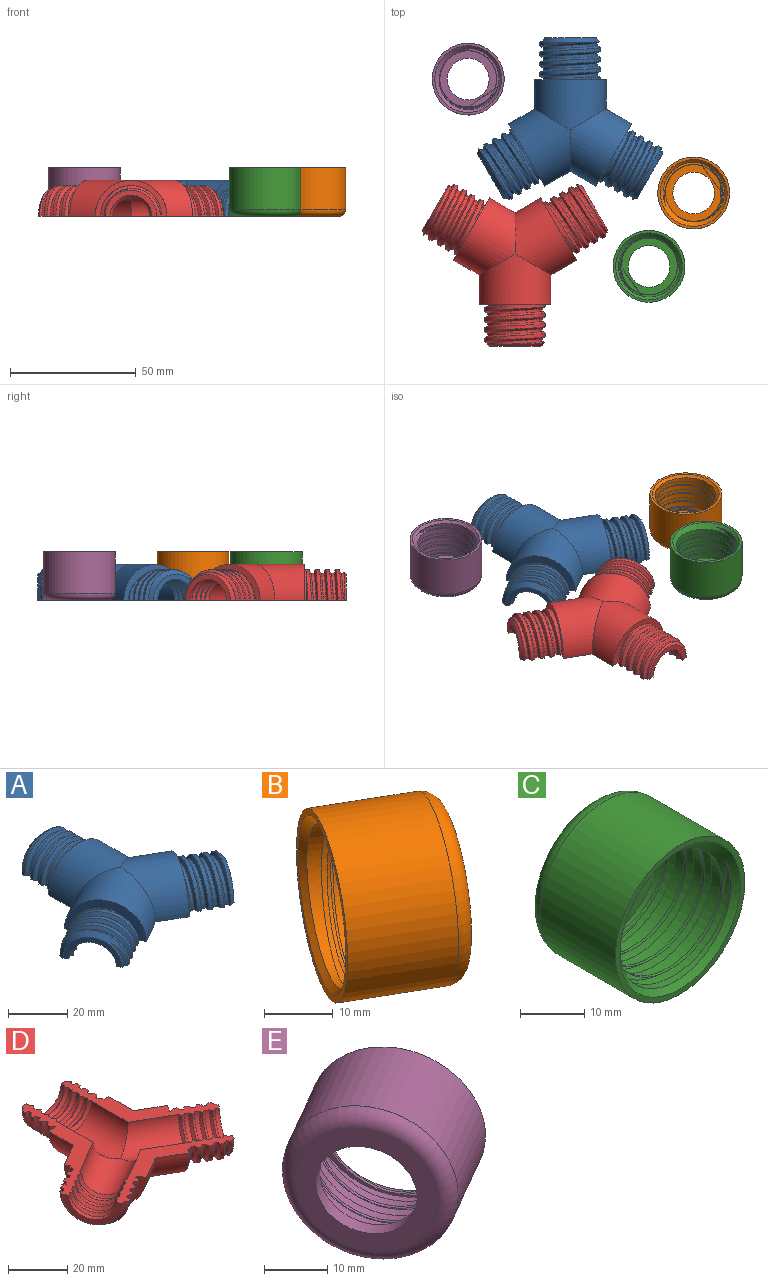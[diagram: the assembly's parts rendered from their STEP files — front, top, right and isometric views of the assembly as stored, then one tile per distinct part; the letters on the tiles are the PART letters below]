
ASSEMBLY  parts=5 mates=4
PART A: 114 faces, bbox 74.6x65.7x25.4 mm
  f0: extruded ~9.1x7.75mm, area 9.1mm2, adj f3,f4,f78,f107
  f1: extruded ~9.1x7.75mm, area 9.1mm2, adj f16,f17,f34,f75
  f2: extruded ~10.12x7.75mm, area 9.1mm2, adj f49,f50,f67,f74
  f3: bspline ~24.86x15.48mm, area 14.4mm2, adj f0,f78,f107,f111
  f4: plane 24.79x14.33mm, normal (-0.87,-0.5,0), area 125.8mm2, adj f0,f77,f78,f107,f111,f113
  f5: cone r=8.3mm half-angle=45deg, axis (0.87,-0.5,0), area 34.7mm2, adj f6,f37,f112,f113
  f6: cone r=7.3mm half-angle=45deg, axis (-0.87,0.5,0), area 34.7mm2, adj f5,f7,f112,f113
  f7: cylinder r=8.3mm len=15.18mm, axis (0.87,-0.5,0), area 41.7mm2, adj f6,f8,f112,f113
  f8: cone r=8.3mm half-angle=45deg, axis (0.87,-0.5,0), area 34.7mm2, adj f7,f9,f112,f113
  f9: cone r=7.3mm half-angle=45deg, axis (-0.87,0.5,0), area 34.7mm2, adj f8,f10,f112,f113
  f10: cylinder r=8.3mm len=15.18mm, axis (0.87,-0.5,0), area 41.7mm2, adj f9,f11,f112,f113
  f11: cone r=8.3mm half-angle=45deg, axis (0.87,-0.5,0), area 34.7mm2, adj f10,f12,f112,f113
  f12: cone r=7.3mm half-angle=45deg, axis (-0.87,0.5,0), area 34.7mm2, adj f11,f13,f112,f113
  f13: cylinder r=8.3mm len=15.18mm, axis (0.87,-0.5,0), area 41.7mm2, adj f12,f14,f112,f113
  f14: cone r=8.3mm half-angle=45deg, axis (0.87,-0.5,0), area 34.7mm2, adj f13,f15,f112,f113
  f15: cone r=7.3mm half-angle=45deg, axis (-0.87,0.5,0), area 34.7mm2, adj f14,f76,f112,f113
  f16: bspline ~24.86x16.81mm, area 14.4mm2, adj f1,f17,f34,f113
  f17: cylinder r=10.8mm len=20.06mm, axis (-0.87,0.5,0), area 40.6mm2, adj f1,f16,f18,f75,f112,f113
  f18: bspline ~24.86x22.64mm, area 58.5mm2, adj f17,f33,f112,f113
  f19: bspline ~24.86x22.47mm, area 60.7mm2, adj f20,f33,f112,f113
  f20: cylinder r=10.8mm len=20.27mm, axis (-0.87,0.5,0), area 38.5mm2, adj f19,f21,f112,f113
  f21: bspline ~24.86x22.64mm, area 58.5mm2, adj f20,f32,f112,f113
  f22: bspline ~24.86x22.47mm, area 60.7mm2, adj f23,f32,f112,f113
  f23: cylinder r=10.8mm len=20.27mm, axis (-0.87,0.5,0), area 38.5mm2, adj f22,f24,f112,f113
  f24: bspline ~24.86x22.64mm, area 58.5mm2, adj f23,f31,f112,f113
  f25: bspline ~21.3x6.91mm, area 8.7mm2, adj f26,f30,f35,f112
  f26: cylinder r=10.8mm len=8.69mm, axis (-0.87,0.5,0), area 3mm2, adj f25,f35,f112
  f27: bspline ~24.86x22.47mm, area 60.7mm2, adj f28,f31,f112,f113
  f28: cylinder r=10.8mm len=20.27mm, axis (-0.87,0.5,0), area 38.5mm2, adj f27,f29,f112,f113
  f29: bspline ~24.86x22.64mm, area 53.3mm2, adj f28,f30,f35,f112,f113
  f30: cylinder r=12.1mm len=17.62mm, axis (0.87,-0.5,0), area 19.1mm2, adj f25,f29,f35,f112
  f31: cylinder r=12.1mm len=22.64mm, axis (0.87,-0.5,0), area 51.9mm2, adj f24,f27,f112,f113
  f32: cylinder r=12.1mm len=22.64mm, axis (0.87,-0.5,0), area 51.9mm2, adj f21,f22,f112,f113
  f33: cylinder r=12.1mm len=22.64mm, axis (0.87,-0.5,0), area 51.9mm2, adj f18,f19,f112,f113
  f34: cylinder r=12.1mm len=2.93mm, axis (0.87,-0.5,0), area 2.2mm2, adj f1,f16,f75,f113
  f35: cone r=10.3mm half-angle=45deg, axis (-0.87,0.5,0), area 76.1mm2, adj f25,f26,f29,f30,f36,f112,f113
  f36: plane 17.84x10.3mm, normal (0.87,-0.5,0), area 58.4mm2, adj f35,f37,f112,f113
  f37: cylinder r=8.3mm len=15.18mm, axis (0.87,-0.5,0), area 41.7mm2, adj f5,f36,f112,f113
  f38: cone r=8.3mm half-angle=45deg, axis (0,1,0), area 34.7mm2, adj f39,f70,f111,f112
  f39: cone r=7.3mm half-angle=45deg, axis (0,-1,0), area 34.7mm2, adj f38,f40,f111,f112
  f40: cylinder r=8.3mm len=16.6mm, axis (0,1,0), area 41.7mm2, adj f39,f41,f111,f112
  f41: cone r=8.3mm half-angle=45deg, axis (0,1,0), area 34.7mm2, adj f40,f42,f111,f112
  f42: cone r=7.3mm half-angle=45deg, axis (0,-1,0), area 34.7mm2, adj f41,f43,f111,f112
  f43: cylinder r=8.3mm len=16.6mm, axis (0,1,0), area 41.7mm2, adj f42,f44,f111,f112
  f44: cone r=8.3mm half-angle=45deg, axis (0,1,0), area 34.7mm2, adj f43,f45,f111,f112
  f45: cone r=7.3mm half-angle=45deg, axis (0,-1,0), area 34.7mm2, adj f44,f46,f111,f112
  f46: cylinder r=8.3mm len=16.6mm, axis (0,1,0), area 41.7mm2, adj f45,f47,f111,f112
  f47: cone r=8.3mm half-angle=45deg, axis (0,1,0), area 34.7mm2, adj f46,f48,f111,f112
  f48: cone r=7.3mm half-angle=45deg, axis (0,-1,0), area 34.7mm2, adj f47,f71,f111,f112
  f49: bspline ~24.86x18.45mm, area 14.4mm2, adj f2,f50,f67,f112
  f50: cylinder r=10.8mm len=21.6mm, axis (0,-1,0), area 40.6mm2, adj f2,f49,f51,f74,f111,f112
  f51: bspline ~24.86x24.6mm, area 58.5mm2, adj f50,f66,f111,f112
  f52: bspline ~24.86x24.6mm, area 60.7mm2, adj f53,f66,f111,f112
  f53: cylinder r=10.8mm len=21.6mm, axis (0,-1,0), area 38.5mm2, adj f52,f54,f111,f112
  f54: bspline ~24.86x24.6mm, area 58.5mm2, adj f53,f65,f111,f112
  f55: bspline ~24.86x24.6mm, area 60.7mm2, adj f56,f65,f111,f112
  f56: cylinder r=10.8mm len=21.6mm, axis (0,-1,0), area 38.5mm2, adj f55,f57,f111,f112
  f57: bspline ~24.86x24.6mm, area 58.5mm2, adj f56,f64,f111,f112
  f58: bspline ~10.65x6.9mm, area 8.7mm2, adj f59,f63,f68,f111
  f59: cylinder r=10.8mm len=8.69mm, axis (0,-1,0), area 3mm2, adj f58,f68,f111
  f60: bspline ~24.86x24.6mm, area 60.7mm2, adj f61,f64,f111,f112
  f61: cylinder r=10.8mm len=21.6mm, axis (0,-1,0), area 38.5mm2, adj f60,f62,f111,f112
  f62: bspline ~24.86x24.6mm, area 53.3mm2, adj f61,f63,f68,f111,f112
  f63: cylinder r=12.1mm len=19.53mm, axis (0,1,0), area 19.1mm2, adj f58,f62,f68,f111
  f64: cylinder r=12.1mm len=24.2mm, axis (0,1,0), area 51.9mm2, adj f57,f60,f111,f112
  f65: cylinder r=12.1mm len=24.2mm, axis (0,1,0), area 51.9mm2, adj f54,f55,f111,f112
  f66: cylinder r=12.1mm len=24.2mm, axis (0,1,0), area 51.9mm2, adj f51,f52,f111,f112
  f67: cylinder r=12.1mm len=2.93mm, axis (0,1,0), area 2.2mm2, adj f2,f49,f74,f112
  f68: cone r=10.3mm half-angle=45deg, axis (0,-1,0), area 76.1mm2, adj f58,f59,f62,f63,f69,f111,f112
  f69: plane 20.6x10.3mm, normal (0,1,0), area 58.4mm2, adj f68,f70,f111,f112
  f70: cylinder r=8.3mm len=16.6mm, axis (0,1,0), area 41.7mm2, adj f38,f69,f111,f112
  f71: cylinder r=8.3mm len=22.27mm, axis (0,1,0), area 518.2mm2, adj f48,f76,f91,f111,f112
  f72: cylinder r=14.3mm len=28.6mm, axis (0,1,0), area 713mm2, adj f73,f74,f77,f111,f112
  f73: cylinder r=14.3mm len=34.77mm, axis (0.87,-0.5,0), area 713mm2, adj f72,f75,f77,f112,f113
  f74: plane 28.63x14.33mm, normal (0,1,0), area 125.8mm2, adj f2,f50,f67,f72,f111,f112
  f75: plane 24.79x14.33mm, normal (0.87,-0.5,0), area 125.8mm2, adj f1,f17,f34,f73,f112,f113
  f76: cylinder r=8.3mm len=27.59mm, axis (0.87,-0.5,0), area 518.2mm2, adj f15,f71,f91,f112,f113
  f77: cylinder r=14.3mm len=34.77mm, axis (-0.87,-0.5,0), area 713mm2, adj f4,f72,f73,f111,f113
  f78: cylinder r=10.8mm len=20.06mm, axis (0.87,0.5,0), area 40.6mm2, adj f0,f3,f4,f79,f111,f113
  f79: bspline ~24.86x20.64mm, area 58.5mm2, adj f78,f106,f111,f113
  f80: cone r=8.3mm half-angle=45deg, axis (-0.87,-0.5,0), area 34.7mm2, adj f81,f110,f111,f113
  f81: cone r=7.3mm half-angle=45deg, axis (0.87,0.5,0), area 34.7mm2, adj f80,f82,f111,f113
  f82: cylinder r=8.3mm len=15.18mm, axis (-0.87,-0.5,0), area 41.7mm2, adj f81,f83,f111,f113
  f83: cone r=8.3mm half-angle=45deg, axis (-0.87,-0.5,0), area 34.7mm2, adj f82,f84,f111,f113
  f84: cone r=7.3mm half-angle=45deg, axis (0.87,0.5,0), area 34.7mm2, adj f83,f85,f111,f113
  f85: cylinder r=8.3mm len=15.18mm, axis (-0.87,-0.5,0), area 41.7mm2, adj f84,f86,f111,f113
  f86: cone r=8.3mm half-angle=45deg, axis (-0.87,-0.5,0), area 34.7mm2, adj f85,f87,f111,f113
  f87: cone r=7.3mm half-angle=45deg, axis (0.87,0.5,0), area 34.7mm2, adj f86,f88,f111,f113
  f88: cylinder r=8.3mm len=15.18mm, axis (-0.87,-0.5,0), area 41.7mm2, adj f87,f89,f111,f113
  f89: cone r=8.3mm half-angle=45deg, axis (-0.87,-0.5,0), area 34.7mm2, adj f88,f90,f111,f113
  f90: cone r=7.3mm half-angle=45deg, axis (0.87,0.5,0), area 34.7mm2, adj f89,f91,f111,f113
  f91: cylinder r=8.3mm len=27.59mm, axis (-0.87,-0.5,0), area 518.2mm2, adj f71,f76,f90,f111,f113
  f92: bspline ~24.86x20.64mm, area 60.7mm2, adj f93,f106,f111,f113
  f93: cylinder r=10.8mm len=20.27mm, axis (0.87,0.5,0), area 38.5mm2, adj f92,f94,f111,f113
  f94: bspline ~24.86x20.64mm, area 58.5mm2, adj f93,f105,f111,f113
  f95: bspline ~24.86x20.64mm, area 60.7mm2, adj f96,f105,f111,f113
  f96: cylinder r=10.8mm len=20.27mm, axis (0.87,0.5,0), area 38.5mm2, adj f95,f97,f111,f113
  f97: bspline ~24.86x20.64mm, area 58.5mm2, adj f96,f104,f111,f113
  f98: bspline ~10.65x5.38mm, area 8.7mm2, adj f99,f103,f108,f113
  f99: cylinder r=10.8mm len=8.69mm, axis (0.87,0.5,0), area 3mm2, adj f98,f108,f113
  f100: bspline ~24.86x20.64mm, area 60.7mm2, adj f101,f104,f111,f113
  f101: cylinder r=10.8mm len=20.27mm, axis (0.87,0.5,0), area 38.5mm2, adj f100,f102,f111,f113
  f102: bspline ~24.86x20.64mm, area 53.3mm2, adj f101,f103,f108,f111,f113
  f103: cylinder r=12.1mm len=17.62mm, axis (-0.87,-0.5,0), area 19.1mm2, adj f98,f102,f108,f113
  f104: cylinder r=12.1mm len=22.64mm, axis (-0.87,-0.5,0), area 51.9mm2, adj f97,f100,f111,f113
  f105: cylinder r=12.1mm len=22.64mm, axis (-0.87,-0.5,0), area 51.9mm2, adj f94,f95,f111,f113
  f106: cylinder r=12.1mm len=22.64mm, axis (-0.87,-0.5,0), area 51.9mm2, adj f79,f92,f111,f113
  f107: cylinder r=12.1mm len=2.93mm, axis (-0.87,-0.5,0), area 2.2mm2, adj f0,f3,f4,f111
  f108: cone r=10.3mm half-angle=45deg, axis (0.87,0.5,0), area 76.1mm2, adj f98,f99,f102,f103,f109,f111,f113
  f109: plane 17.84x10.3mm, normal (-0.87,-0.5,0), area 58.4mm2, adj f108,f110,f111,f113
  f110: cylinder r=8.3mm len=15.18mm, axis (-0.87,-0.5,0), area 41.7mm2, adj f80,f109,f111,f113
  f111: plane 48.28x30.07mm, normal (0,0,-1), area 274.3mm2, adj f3,f4,f38,f39,f40,f41,f42,f43
  f112: plane 48.28x30.07mm, normal (0,0,-1), area 274.3mm2, adj f5,f6,f7,f8,f9,f10,f11,f12
  f113: plane 55.68x18.77mm, normal (0,0,-1), area 274.3mm2, adj f4,f5,f6,f7,f8,f9,f10,f11
PART B: 11 faces, bbox 30.5x34.4x31 mm
  f0: cylinder r=12.3mm len=29.14mm, axis (0.87,-0.5,0), area 682.7mm2, adj f4,f7,f10
  f1: torus R=11.74mm, axis (0.87,-0.5,0), area 338mm2, adj f2,f6
  f2: cylinder r=14.3mm len=33.1mm, axis (0.87,-0.5,0), area 1497.7mm2, adj f1,f3
  f3: plane 28.6x24.77mm, normal (-0.87,0.5,0), area 86.7mm2, adj f2,f10
  f4: plane 24x20.08mm, normal (-0.87,0.5,0), area 224mm2, adj f0,f5,f7,f8,f9
  f5: cylinder r=8.3mm len=16.6mm, axis (0.87,-0.5,0), area 133.6mm2, adj f4,f6
  f6: plane 23.48x20.33mm, normal (0.87,-0.5,0), area 216.4mm2, adj f1,f5
  f7: bspline ~11.79x8.2mm, area 6.6mm2, adj f0,f4,f8
  f8: extruded ~8.97x1.47mm, area 3.1mm2, adj f4,f7,f9
  f9: cylinder r=11.3mm len=26.91mm, axis (-0.87,0.5,0), area 151.3mm2, adj f4,f8,f10
  f10: cone r=15.3mm half-angle=45deg, axis (-0.87,0.5,0), area 143.6mm2, adj f0,f3,f9
PART C: 11 faces, bbox 31x19.2x31 mm
  f0: cylinder r=12.3mm len=24.6mm, axis (0,1,0), area 682.7mm2, adj f4,f7,f10
  f1: torus R=11.74mm, axis (0,1,0), area 338mm2, adj f2,f6
  f2: cylinder r=14.3mm len=28.6mm, axis (0,1,0), area 1497.7mm2, adj f1,f3
  f3: plane 28.6x28.6mm, normal (0,-1,0), area 86.7mm2, adj f2,f10
  f4: plane 24x23.17mm, normal (0,-1,0), area 224mm2, adj f0,f5,f7,f8,f9
  f5: cylinder r=8.3mm len=16.6mm, axis (0,1,0), area 133.6mm2, adj f4,f6
  f6: plane 23.48x23.48mm, normal (0,1,0), area 216.4mm2, adj f1,f5
  f7: bspline ~11.79x9.22mm, area 6.6mm2, adj f0,f4,f8
  f8: extruded ~8.97x1.42mm, area 3.1mm2, adj f4,f7,f9
  f9: cylinder r=11.3mm len=22.6mm, axis (0,-1,0), area 151.3mm2, adj f4,f8,f10
  f10: cone r=15.3mm half-angle=45deg, axis (0,-1,0), area 143.6mm2, adj f0,f3,f9
PART D: 111 faces, bbox 76.4x67.5x25.4 mm
  f0: cylinder r=8.3mm len=15.18mm, axis (-0.87,-0.5,0), area 41.7mm2, adj f1,f18,f108,f110
  f1: plane 17.84x10.3mm, normal (-0.87,-0.5,0), area 58.4mm2, adj f0,f2,f108,f110
  f2: cone r=10.3mm half-angle=45deg, axis (0.87,0.5,0), area 40.3mm2, adj f1,f19,f24,f108,f110
  f3: cylinder r=12.1mm len=22.64mm, axis (-0.87,-0.5,0), area 51.9mm2, adj f20,f29,f108,f110
  f4: cylinder r=12.1mm len=22.64mm, axis (-0.87,-0.5,0), area 51.9mm2, adj f21,f30,f108,f110
  f5: cylinder r=12.1mm len=22.64mm, axis (-0.87,-0.5,0), area 51.9mm2, adj f22,f31,f108,f110
  f6: cylinder r=12.1mm len=22.37mm, axis (-0.87,-0.5,0), area 53.2mm2, adj f23,f32,f34,f105,f108,f110
  f7: cylinder r=8.3mm len=27.59mm, axis (-0.87,-0.5,0), area 518.2mm2, adj f8,f35,f38,f108,f110
  f8: cone r=7.3mm half-angle=45deg, axis (0.87,0.5,0), area 34.7mm2, adj f7,f9,f108,f110
  f9: cone r=8.3mm half-angle=45deg, axis (-0.87,-0.5,0), area 34.7mm2, adj f8,f10,f108,f110
  f10: cylinder r=8.3mm len=15.18mm, axis (-0.87,-0.5,0), area 41.7mm2, adj f9,f11,f108,f110
  f11: cone r=7.3mm half-angle=45deg, axis (0.87,0.5,0), area 34.7mm2, adj f10,f12,f108,f110
  f12: cone r=8.3mm half-angle=45deg, axis (-0.87,-0.5,0), area 34.7mm2, adj f11,f13,f108,f110
  f13: cylinder r=8.3mm len=15.18mm, axis (-0.87,-0.5,0), area 41.7mm2, adj f12,f14,f108,f110
  f14: cone r=7.3mm half-angle=45deg, axis (0.87,0.5,0), area 34.7mm2, adj f13,f15,f108,f110
  f15: cone r=8.3mm half-angle=45deg, axis (-0.87,-0.5,0), area 34.7mm2, adj f14,f16,f108,f110
  f16: cylinder r=8.3mm len=15.18mm, axis (-0.87,-0.5,0), area 41.7mm2, adj f15,f17,f108,f110
  f17: cone r=7.3mm half-angle=45deg, axis (0.87,0.5,0), area 34.7mm2, adj f16,f18,f108,f110
  f18: cone r=8.3mm half-angle=45deg, axis (-0.87,-0.5,0), area 34.7mm2, adj f0,f17,f108,f110
  f19: bspline ~24.86x22.47mm, area 13.8mm2, adj f2,f24,f108
  f20: bspline ~24.86x22.64mm, area 60.7mm2, adj f3,f25,f108,f110
  f21: bspline ~24.86x22.64mm, area 60.7mm2, adj f4,f26,f108,f110
  f22: bspline ~24.86x22.64mm, area 60.7mm2, adj f5,f27,f108,f110
  f23: bspline ~24.86x16.81mm, area 12.1mm2, adj f6,f28,f105,f110
  f24: cylinder r=10.8mm len=20.01mm, axis (0.87,0.5,0), area 36mm2, adj f2,f19,f29,f108,f110
  f25: cylinder r=10.8mm len=20.27mm, axis (0.87,0.5,0), area 38.5mm2, adj f20,f30,f108,f110
  f26: cylinder r=10.8mm len=20.27mm, axis (0.87,0.5,0), area 38.5mm2, adj f21,f31,f108,f110
  f27: cylinder r=10.8mm len=20.27mm, axis (0.87,0.5,0), area 38.5mm2, adj f22,f32,f108,f110
  f28: cylinder r=10.8mm len=0.63mm, axis (0.87,0.5,0), area 0.4mm2, adj f23,f34,f105,f110
  f29: bspline ~24.86x22.47mm, area 58.5mm2, adj f3,f24,f108,f110
  f30: bspline ~24.86x22.47mm, area 58.5mm2, adj f4,f25,f108,f110
  f31: bspline ~24.86x22.47mm, area 58.5mm2, adj f5,f26,f108,f110
  f32: bspline ~24.86x22.47mm, area 58.5mm2, adj f6,f27,f108,f110
  f33: cylinder r=14.3mm len=34.77mm, axis (-0.87,-0.5,0), area 713mm2, adj f34,f39,f40,f108,f110
  f34: plane 24.78x14.32mm, normal (-0.87,-0.5,0), area 101mm2, adj f6,f28,f33,f105,f108,f110
  f35: cylinder r=8.3mm len=27.59mm, axis (0.87,-0.5,0), area 518.2mm2, adj f7,f38,f48,f109,f110
  f36: plane 24.78x14.32mm, normal (0.87,-0.5,0), area 101mm2, adj f39,f47,f68,f106,f109,f110
  f37: plane 28.62x14.32mm, normal (0,1,0), area 101mm2, adj f40,f79,f100,f107,f108,f109
  f38: cylinder r=8.3mm len=22.27mm, axis (0,1,0), area 518.2mm2, adj f7,f35,f80,f108,f109
  f39: cylinder r=14.3mm len=34.77mm, axis (0.87,-0.5,0), area 713mm2, adj f33,f36,f40,f109,f110
  f40: cylinder r=14.3mm len=28.6mm, axis (0,1,0), area 713mm2, adj f33,f37,f39,f108,f109
  f41: cylinder r=8.3mm len=15.18mm, axis (0.87,-0.5,0), area 41.7mm2, adj f42,f58,f109,f110
  f42: plane 17.84x10.3mm, normal (0.87,-0.5,0), area 58.4mm2, adj f41,f43,f109,f110
  f43: cone r=10.3mm half-angle=45deg, axis (-0.87,0.5,0), area 40.3mm2, adj f42,f59,f64,f109,f110
  f44: cylinder r=12.1mm len=22.64mm, axis (0.87,-0.5,0), area 51.9mm2, adj f60,f69,f109,f110
  f45: cylinder r=12.1mm len=22.64mm, axis (0.87,-0.5,0), area 51.9mm2, adj f61,f70,f109,f110
  f46: cylinder r=12.1mm len=22.64mm, axis (0.87,-0.5,0), area 51.9mm2, adj f62,f71,f109,f110
  f47: cylinder r=12.1mm len=22.37mm, axis (0.87,-0.5,0), area 53.2mm2, adj f36,f63,f72,f106,f109,f110
  f48: cone r=7.3mm half-angle=45deg, axis (-0.87,0.5,0), area 34.7mm2, adj f35,f49,f109,f110
  f49: cone r=8.3mm half-angle=45deg, axis (0.87,-0.5,0), area 34.7mm2, adj f48,f50,f109,f110
  f50: cylinder r=8.3mm len=15.18mm, axis (0.87,-0.5,0), area 41.7mm2, adj f49,f51,f109,f110
  f51: cone r=7.3mm half-angle=45deg, axis (-0.87,0.5,0), area 34.7mm2, adj f50,f52,f109,f110
  f52: cone r=8.3mm half-angle=45deg, axis (0.87,-0.5,0), area 34.7mm2, adj f51,f53,f109,f110
  f53: cylinder r=8.3mm len=15.18mm, axis (0.87,-0.5,0), area 41.7mm2, adj f52,f54,f109,f110
  f54: cone r=7.3mm half-angle=45deg, axis (-0.87,0.5,0), area 34.7mm2, adj f53,f55,f109,f110
  f55: cone r=8.3mm half-angle=45deg, axis (0.87,-0.5,0), area 34.7mm2, adj f54,f56,f109,f110
  f56: cylinder r=8.3mm len=15.18mm, axis (0.87,-0.5,0), area 41.7mm2, adj f55,f57,f109,f110
  f57: cone r=7.3mm half-angle=45deg, axis (-0.87,0.5,0), area 34.7mm2, adj f56,f58,f109,f110
  f58: cone r=8.3mm half-angle=45deg, axis (0.87,-0.5,0), area 34.7mm2, adj f41,f57,f109,f110
  f59: bspline ~24.86x20.64mm, area 13.8mm2, adj f43,f64,f110
  f60: bspline ~24.86x20.64mm, area 60.7mm2, adj f44,f65,f109,f110
  f61: bspline ~24.86x20.64mm, area 60.7mm2, adj f45,f66,f109,f110
  f62: bspline ~24.86x20.64mm, area 60.7mm2, adj f46,f67,f109,f110
  f63: bspline ~24.86x15.48mm, area 12.1mm2, adj f47,f68,f106,f109
  f64: cylinder r=10.8mm len=20.01mm, axis (-0.87,0.5,0), area 36mm2, adj f43,f59,f69,f109,f110
  f65: cylinder r=10.8mm len=20.27mm, axis (-0.87,0.5,0), area 38.5mm2, adj f60,f70,f109,f110
  f66: cylinder r=10.8mm len=20.27mm, axis (-0.87,0.5,0), area 38.5mm2, adj f61,f71,f109,f110
  f67: cylinder r=10.8mm len=20.27mm, axis (-0.87,0.5,0), area 38.5mm2, adj f62,f72,f109,f110
  f68: cylinder r=10.8mm len=0.63mm, axis (-0.87,0.5,0), area 0.4mm2, adj f36,f63,f106,f109
  f69: bspline ~24.86x20.64mm, area 58.5mm2, adj f44,f64,f109,f110
  f70: bspline ~24.86x20.64mm, area 58.5mm2, adj f45,f65,f109,f110
  f71: bspline ~24.86x20.64mm, area 58.5mm2, adj f46,f66,f109,f110
  f72: bspline ~24.86x20.64mm, area 58.5mm2, adj f47,f67,f109,f110
  f73: cylinder r=8.3mm len=16.6mm, axis (0,1,0), area 41.7mm2, adj f74,f90,f108,f109
  f74: plane 20.6x10.3mm, normal (0,1,0), area 58.4mm2, adj f73,f75,f108,f109
  f75: cone r=10.3mm half-angle=45deg, axis (0,-1,0), area 40.3mm2, adj f74,f91,f96,f108,f109
  f76: cylinder r=12.1mm len=24.2mm, axis (0,1,0), area 51.9mm2, adj f92,f101,f108,f109
  f77: cylinder r=12.1mm len=24.2mm, axis (0,1,0), area 51.9mm2, adj f93,f102,f108,f109
  f78: cylinder r=12.1mm len=24.2mm, axis (0,1,0), area 51.9mm2, adj f94,f103,f108,f109
  f79: cylinder r=12.1mm len=24.2mm, axis (0,1,0), area 53.2mm2, adj f37,f95,f104,f107,f108,f109
  f80: cone r=7.3mm half-angle=45deg, axis (0,-1,0), area 34.7mm2, adj f38,f81,f108,f109
  f81: cone r=8.3mm half-angle=45deg, axis (0,1,0), area 34.7mm2, adj f80,f82,f108,f109
  f82: cylinder r=8.3mm len=16.6mm, axis (0,1,0), area 41.7mm2, adj f81,f83,f108,f109
  f83: cone r=7.3mm half-angle=45deg, axis (0,-1,0), area 34.7mm2, adj f82,f84,f108,f109
  f84: cone r=8.3mm half-angle=45deg, axis (0,1,0), area 34.7mm2, adj f83,f85,f108,f109
  f85: cylinder r=8.3mm len=16.6mm, axis (0,1,0), area 41.7mm2, adj f84,f86,f108,f109
  f86: cone r=7.3mm half-angle=45deg, axis (0,-1,0), area 34.7mm2, adj f85,f87,f108,f109
  f87: cone r=8.3mm half-angle=45deg, axis (0,1,0), area 34.7mm2, adj f86,f88,f108,f109
  f88: cylinder r=8.3mm len=16.6mm, axis (0,1,0), area 41.7mm2, adj f87,f89,f108,f109
  f89: cone r=7.3mm half-angle=45deg, axis (0,-1,0), area 34.7mm2, adj f88,f90,f108,f109
  f90: cone r=8.3mm half-angle=45deg, axis (0,1,0), area 34.7mm2, adj f73,f89,f108,f109
  f91: bspline ~24.86x24.6mm, area 13.8mm2, adj f75,f96,f109
  f92: bspline ~24.86x24.6mm, area 60.7mm2, adj f76,f97,f108,f109
  f93: bspline ~24.86x24.6mm, area 60.7mm2, adj f77,f98,f108,f109
  f94: bspline ~24.86x24.6mm, area 60.7mm2, adj f78,f99,f108,f109
  f95: bspline ~24.86x18.45mm, area 12.1mm2, adj f79,f100,f107,f108
  f96: cylinder r=10.8mm len=21.6mm, axis (0,-1,0), area 36mm2, adj f75,f91,f101,f108,f109
  f97: cylinder r=10.8mm len=21.6mm, axis (0,-1,0), area 38.5mm2, adj f92,f102,f108,f109
  f98: cylinder r=10.8mm len=21.6mm, axis (0,-1,0), area 38.5mm2, adj f93,f103,f108,f109
  f99: cylinder r=10.8mm len=21.6mm, axis (0,-1,0), area 38.5mm2, adj f94,f104,f108,f109
  f100: cylinder r=10.8mm len=0.7mm, axis (0,-1,0), area 0.4mm2, adj f37,f95,f107,f108
  f101: bspline ~24.86x24.6mm, area 58.5mm2, adj f76,f96,f108,f109
  f102: bspline ~24.86x24.6mm, area 58.5mm2, adj f77,f97,f108,f109
  f103: bspline ~24.86x24.6mm, area 58.5mm2, adj f78,f98,f108,f109
  f104: bspline ~24.86x24.6mm, area 58.5mm2, adj f79,f99,f108,f109
  f105: extruded ~10.83x6.29mm, area 9.1mm2, adj f6,f23,f28,f34
  f106: extruded ~10.83x6.29mm, area 9.1mm2, adj f36,f47,f63,f68
  f107: extruded ~10.83x6.88mm, area 9.1mm2, adj f37,f79,f95,f100
  f108: plane 48.28x30.07mm, normal (0,0,1), area 274.3mm2, adj f0,f1,f2,f3,f4,f5,f6,f7
  f109: plane 48.28x30.07mm, normal (0,0,1), area 274.3mm2, adj f35,f36,f37,f38,f39,f40,f41,f42
  f110: plane 55.68x18.77mm, normal (0,0,1), area 274.3mm2, adj f0,f1,f2,f3,f4,f5,f6,f7
PART E: 11 faces, bbox 30.5x34.4x31 mm
  f0: cylinder r=12.3mm len=29.14mm, axis (-0.87,-0.5,0), area 682.7mm2, adj f4,f7,f10
  f1: torus R=11.74mm, axis (-0.87,-0.5,0), area 338mm2, adj f2,f6
  f2: cylinder r=14.3mm len=33.1mm, axis (-0.87,-0.5,0), area 1497.7mm2, adj f1,f3
  f3: plane 28.6x24.77mm, normal (0.87,0.5,0), area 86.7mm2, adj f2,f10
  f4: plane 24x20.08mm, normal (0.87,0.5,0), area 224mm2, adj f0,f5,f7,f8,f9
  f5: cylinder r=8.3mm len=16.6mm, axis (-0.87,-0.5,0), area 133.6mm2, adj f4,f6
  f6: plane 23.48x20.33mm, normal (-0.87,-0.5,0), area 216.4mm2, adj f1,f5
  f7: bspline ~11.79x7.93mm, area 6.6mm2, adj f0,f4,f8
  f8: extruded ~8.97x1.14mm, area 3.1mm2, adj f4,f7,f9
  f9: cylinder r=11.3mm len=26.91mm, axis (0.87,0.5,0), area 151.3mm2, adj f4,f8,f10
  f10: cone r=15.3mm half-angle=45deg, axis (0.87,0.5,0), area 143.6mm2, adj f0,f3,f9
PLACE A t=(-51.07,133.72,-23.67)mm
PLACE B rot(axis=(0.77,0.45,-0.45),104.5deg) t=(29.9,71.89,33.89)mm
PLACE C rot(axis=(-1,0,0),90deg) t=(-19.66,42.67,-21.11)mm fixed
PLACE D rot(axis=(1,0,0),180deg) t=(-73.02,10.87,-23.67)mm
PLACE E rot(axis=(0.25,-0.94,-0.25),93.8deg) t=(-91.68,149,33.89)mm
MATE planar B.f1 <-> C.f0  axis (0,0,-1) through (-1.86,71.89,-23.67)mm
MATE planar A.f112 <-> C.f0  axis (0,0,-1) through (-36.77,105.31,-23.67)mm
MATE planar D.f109 <-> C.f0  axis (0,0,-1) through (-58.72,39.28,-23.67)mm
MATE planar C.f0 <-> E.f1  axis (0,0,-1) through (-19.66,42.67,-23.67)mm
